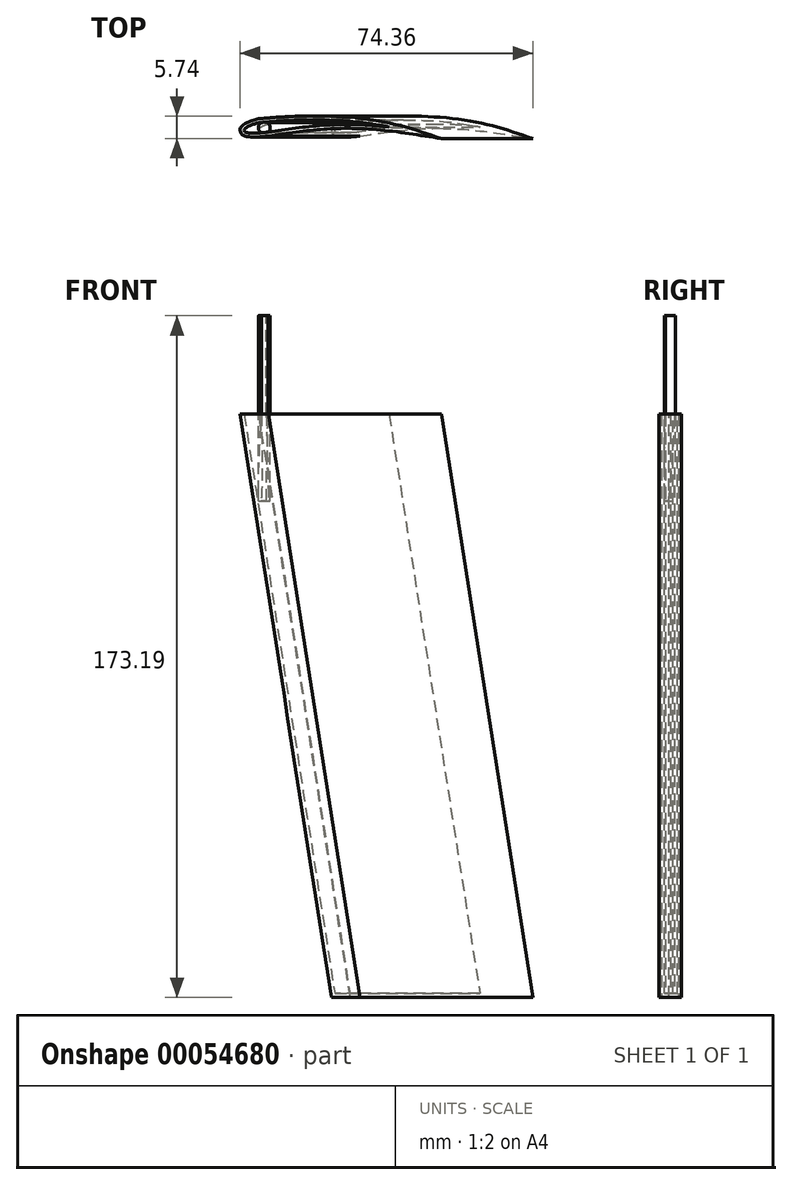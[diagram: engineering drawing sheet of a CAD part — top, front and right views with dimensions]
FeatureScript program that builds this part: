
annotation { "Feature Type Name" : "Feature", "Feature Type Description" : "" }
export const myFeature = defineFeature(function(context is Context, id is Id, definition is map)
    precondition{}
    {
        {
            var Q0;
            Q0=qCreatedBy(makeId("Top.planeOp"),FACE);
            var sketch = newSketch(context, id + "F0", { "sketchPlane" : qUnion([Q0])});
            skFitSpline(sketch, "E0", {"points": [v(-24.09, 0) * mm, v(0, 2.63) * mm, v(23.9, 0) * mm], "startDerivative": vector(48.13, 7.87) * mm, "endDerivative": vector(47.84, -7.88) * mm});
            skFitSpline(sketch, "E1", {"points": [v(23.9, 0) * mm, v(7.25, 4.63) * mm, v(-12.87, 5.68) * mm, v(-22.58, 5.04) * mm], "startDerivative": vector(-44.42, 15.41) * mm, "endDerivative": vector(-32.73, -2.96) * mm});
            skFitSpline(sketch, "E2", {"points": [v(-22.58, 5.04) * mm, v(-24.34, 4.55) * mm, v(-26.44, 3.51) * mm, v(-27.21, 2.5) * mm, v(-26.93, 1.21) * mm, v(-24.71, 0.43) * mm, v(-20.03, 0.66) * mm], "startDerivative": vector(-11, -2.64) * mm, "endDerivative": vector(20.31, 1.92) * mm});
            skSolve(sketch);
        }
        {
            var Q0;
            Q0=qCreatedBy(makeId("Front.planeOp"),FACE);
            var sketch = newSketch(context, id + "F1", { "sketchPlane" : qUnion([Q0])});
            skLineSegment(sketch, "E3", {"start": v(-27.45, 0) * mm, "end": v(-4.24, -148.2) * mm});
            skPoint(sketch, "E4.start.orphan", {"position": v(23.8, 0) * mm});
            skSolve(sketch);
        }
        {
            var Q0;
            Q0=makeQuery(id+"F0.imprint","IMPRINT",FACE,{"disambiguationData":[TD([[makeQuery(id+"F0.imprint","IMPRINT",EDGE,{"derivedFrom":sQuery(id+"F0.wireOp",EDGE,"E0")}),1.0]])]});
            var Q1;
            Q1=sQuery(id+"F1.wireOp",EDGE,"E3");
            sweep(context, id + "F2", {"profiles" : qUnion([Q0]), "path" : qUnion([Q1])});
        }
        {
            var Q0;
            Q0=makeQuery(id+"F2.opSweep","CAP_FACE",FACE,{"disambiguationData":[OSD([sQuery(id+"F0.wireOp",EDGE,"E0"),sQuery(id+"F0.wireOp",EDGE,"E1"),sQuery(id+"F0.wireOp",EDGE,"E2"),sQuery(id+"F1.wireOp",VERTEX,"E3.start")])],"isStart":true});
            shell(context, id + "F3", {"entities" : qUnion([Q0]), "thickness" : 1 * mm});
        }
        {
            var Q0;
            Q0=makeQuery(id+"F2.opSweep","CAP_FACE",FACE,{"disambiguationData":[OSD([sQuery(id+"F0.wireOp",EDGE,"E0"),sQuery(id+"F0.wireOp",EDGE,"E1"),sQuery(id+"F0.wireOp",EDGE,"E2"),sQuery(id+"F1.wireOp",VERTEX,"E3.start")])],"isStart":true});
            var sketch = newSketch(context, id + "F4", { "sketchPlane" : qUnion([Q0])});
            skCircle(sketch, "E5", {"center": v(-21.11, 2.8) * mm, "radius": 1.5 * mm});
            skSolve(sketch);
        }
        {
            var Q0;
            {var subQ0=sQuery(id+"F4.wireOp",EDGE,"E5");var subQ1=sQuery(id+"F1.wireOp",VERTEX,"E3.start");var subQ2=makeQuery(id+"F3.opShell","OFFSET_EDGE",EDGE,{"disambiguationData":[OSD([sQuery(id+"F0.wireOp",EDGE,"E1"),subQ1])]});var subQ3=makeQuery(id+"F4.imprint","INTERSECT",VERTEX,{"disambiguationData":[OD(0.0)],"derivedFrom":[subQ2,subQ0]});Q0=makeQuery(id+"F4.imprint","IMPRINT",FACE,{"disambiguationData":[TD([[makeQuery(id+"F4.imprint","IMPRINT",EDGE,{"disambiguationData":[TD([[subQ3,-1.0]])],"derivedFrom":subQ0}),1.0]])]});}
            var Q1;
            {var subQ0=sQuery(id+"F4.wireOp",EDGE,"E5");var subQ1=makeQuery(id+"F3.opShell","OFFSET_EDGE",EDGE,{"disambiguationData":[OSD([sQuery(id+"F0.wireOp",EDGE,"E1"),sQuery(id+"F1.wireOp",VERTEX,"E3.start")])]});var subQ2=makeQuery(id+"F4.imprint","INTERSECT",VERTEX,{"disambiguationData":[OD(0.0)],"derivedFrom":[subQ1,subQ0]});Q1=makeQuery(id+"F4.imprint","IMPRINT",FACE,{"disambiguationData":[TD([[makeQuery(id+"F4.imprint","IMPRINT",EDGE,{"disambiguationData":[TD([[subQ2,1.0]])],"derivedFrom":subQ0}),1.0]])]});}
            var Q2;
            {var subQ0=sQuery(id+"F4.wireOp",EDGE,"E5");var subQ1=sQuery(id+"F1.wireOp",VERTEX,"E3.start");var subQ2=makeQuery(id+"F3.opShell","OFFSET_EDGE",EDGE,{"disambiguationData":[OSD([sQuery(id+"F0.wireOp",EDGE,"E2"),subQ1])]});var subQ3=makeQuery(id+"F4.imprint","INTERSECT",VERTEX,{"derivedFrom":[subQ2,subQ0]});Q2=makeQuery(id+"F4.imprint","IMPRINT",FACE,{"disambiguationData":[TD([[makeQuery(id+"F4.imprint","IMPRINT",EDGE,{"disambiguationData":[TD([[subQ3,-1.0]])],"derivedFrom":subQ0}),1.0]])]});}
            extrude(context, id + "F5", {"entities" : qUnion([Q0, Q1, Q2]), "operationType" : NewBodyOperationType.ADD, "oppositeDirection" : true, "depth" : 22 * mm});
        }
        {
            var Q0;
            {var subQ0=sQuery(id+"F4.wireOp",EDGE,"E5");var subQ1=sQuery(id+"F1.wireOp",VERTEX,"E3.start");var subQ2=makeQuery(id+"F3.opShell","OFFSET_EDGE",EDGE,{"disambiguationData":[OSD([sQuery(id+"F0.wireOp",EDGE,"E1"),subQ1])]});var subQ3=makeQuery(id+"F4.imprint","INTERSECT",VERTEX,{"disambiguationData":[OD(0.0)],"derivedFrom":[subQ2,subQ0]});Q0=makeQuery(id+"F4.imprint","IMPRINT",FACE,{"disambiguationData":[TD([[makeQuery(id+"F4.imprint","IMPRINT",EDGE,{"disambiguationData":[TD([[subQ3,-1.0]])],"derivedFrom":subQ0}),1.0]])]});}
            extrude(context, id + "F6", {"entities" : qUnion([Q0]), "operationType" : NewBodyOperationType.ADD, "depth" : 25 * mm});
        }
    });
